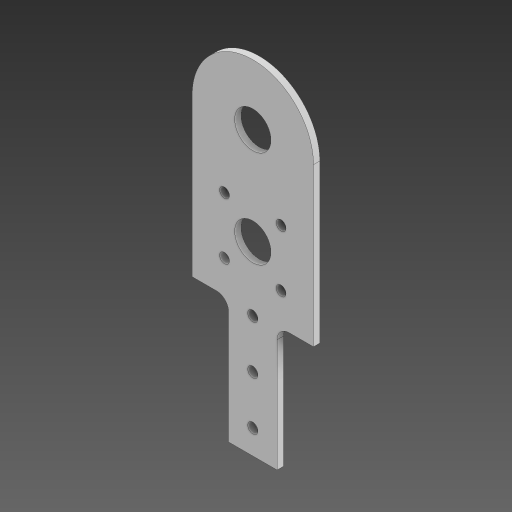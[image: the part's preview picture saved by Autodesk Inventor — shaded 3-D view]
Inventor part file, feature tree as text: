
AUTODESK INVENTOR PART (.ipt)
format: ipt  version: 2024 (Build 280153000, 153)  size: 235,520 bytes
history: native  units: in
note: dims shown in document units (in); Inventor stores cm internally (conversion verified against a paired STEP export)
features: fillet x4, sketch x2, other x1, extrude x1, hole x1
ambient origin geometry x8: Origin, YZ Plane, XZ Plane, XY Plane, X Axis, Y Axis, Z Axis, Center Point
bodies: Solid1 (feature_tree)
feature tree (9):
  other  "wrist plate 2"
  sketch  "Sketch1"  dims[d0=2.5in d1=5.0in d3=4.575in d4=1.25in]
  extrude  "Extrusion1"  Depth=1.25in
  fillet  "Fillet1"  Radius=4.575in
  fillet  "Fillet2"  Radius=1.25in
  hole  "Hole1"  [1 undecoded]
  fillet  "Fillet5"  Radius=1.25in
  fillet  "Fillet6"  Radius=1.25in
  sketch  "Sketch3"  dims[d5=3.25in d6=0.13in d7=0.0in d8=1.25in d9=1.25in d12=0.748in d13=0.748in d14=0.209in d16=1.65in d17=0.201in d18=0.75in d19=0.385in d20=0.25in d21=0.5635in d22=0.64in d23=0.8108in d28=135.0deg d29=1.0in d30=1.0in d31=1.0in d32=1.0in d33=2.0in d34=0.25in d35=0.25in d36=0.5in]
note: 1 required parameter value undecoded (feature->parameter linkage not recoverable at this tier; creation-order binding heuristic only, values carry confidence <= 0.55)
